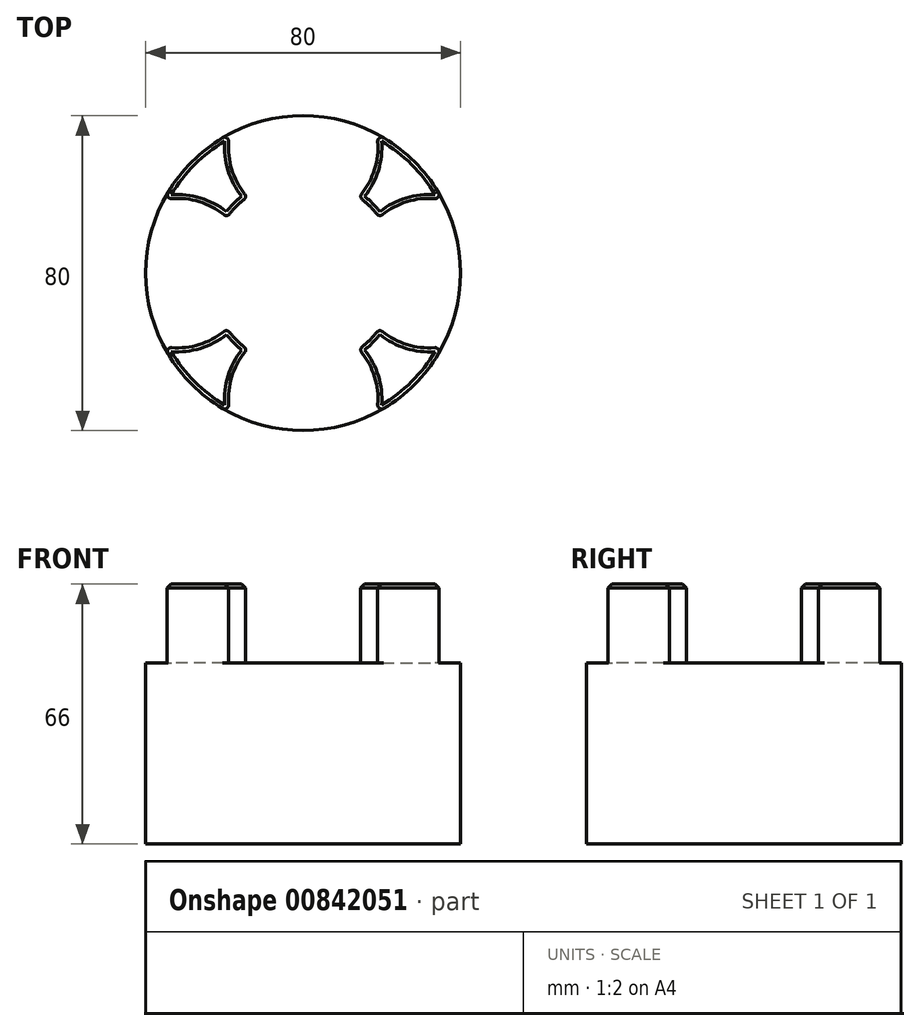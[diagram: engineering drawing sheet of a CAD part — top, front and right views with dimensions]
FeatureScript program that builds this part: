
annotation { "Feature Type Name" : "Feature", "Feature Type Description" : "" }
export const myFeature = defineFeature(function(context is Context, id is Id, definition is map)
    precondition{}
    {
        {
            var Q0;
            Q0=qCreatedBy(makeId("Top.planeOp"),FACE);
            var sketch = newSketch(context, id + "F0", { "sketchPlane" : qUnion([Q0])});
            skCircle(sketch, "E0", {"center": v(0, 0) * mm, "radius": 40 * mm});
            skSolve(sketch);
        }
        {
            var Q0;
            Q0=makeQuery(id+"F0.imprint","IMPRINT",FACE,{"disambiguationData":[TD([[makeQuery(id+"F0.imprint","IMPRINT",EDGE,{"derivedFrom":sQuery(id+"F0.wireOp",EDGE,"E0")}),1.0]])]});
            extrude(context, id + "F1", {"entities" : qUnion([Q0]), "depth" : 66 * mm, "offsetDistance" : 25 * mm});
        }
        {
            var Q0;
            Q0=makeQuery(id+"F1.opExtrude","CAP_FACE",FACE,{"disambiguationData":[OSD([sQuery(id+"F0.wireOp",EDGE,"E0")])],"isStart":false});
            var sketch = newSketch(context, id + "F2", { "sketchPlane" : qUnion([Q0])});
            skCircle(sketch, "E1", {"center": v(0, 0) * mm, "radius": 24 * mm});
            skSolve(sketch);
        }
        {
            var Q0;
            Q0=makeQuery(id+"F2.imprint","IMPRINT",FACE,{"disambiguationData":[TD([[makeQuery(id+"F2.imprint","IMPRINT",EDGE,{"derivedFrom":sQuery(id+"F2.wireOp",EDGE,"E1")}),1.0]])]});
            extrude(context, id + "F3", {"entities" : qUnion([Q0]), "operationType" : NewBodyOperationType.REMOVE, "oppositeDirection" : true, "depth" : 20 * mm, "offsetDistance" : 25 * mm});
        }
        {
            var Q0;
            Q0=makeQuery(id+"F1.opExtrude","CAP_FACE",FACE,{"disambiguationData":[OSD([sQuery(id+"F0.wireOp",EDGE,"E0")])],"isStart":false});
            var sketch = newSketch(context, id + "F4", { "sketchPlane" : qUnion([Q0])});
            skCircle(sketch, "E2", {"center": v(32, 0) * mm, "radius": 19 * mm});
            skCircle(sketch, "E3.1.0", {"center": v(0, 32) * mm, "radius": 19 * mm});
            skCircle(sketch, "E3.2.0", {"center": v(-32, 0) * mm, "radius": 19 * mm});
            skCircle(sketch, "E3.3.0", {"center": v(0, -32) * mm, "radius": 19 * mm});
            skPoint(sketch, "E3.center", {"position": v(0, 0) * mm});
            skSolve(sketch);
        }
        {
            var Q0;
            Q0 = qSketchRegion(id + "F4", true);
            extrude(context, id + "F5", {"entities" : qUnion([Q0]), "operationType" : NewBodyOperationType.REMOVE, "oppositeDirection" : true, "depth" : 20 * mm, "offsetDistance" : 25 * mm});
        }
        {
            var Q0;
            Q0=makeQuery(id+"F5.boolean.opBoolean","INTERSECT",EDGE,{"disambiguationData":[OD(1.0)],"derivedFrom":[makeQuery(id+"F1.opExtrude","SWEPT_FACE",FACE,{"disambiguationData":[OSD([sQuery(id+"F0.wireOp",EDGE,"E0")])]}),makeQuery(id+"F5.opExtrude","SWEPT_FACE",FACE,{"disambiguationData":[OSD([sQuery(id+"F4.wireOp",EDGE,"E3.1.0")])]})]});
            var Q1;
            Q1=makeQuery(id+"F5.boolean.opBoolean","INTERSECT",EDGE,{"disambiguationData":[OD(1.0)],"derivedFrom":[makeQuery(id+"F1.opExtrude","SWEPT_FACE",FACE,{"disambiguationData":[OSD([sQuery(id+"F0.wireOp",EDGE,"E0")])]}),makeQuery(id+"F5.opExtrude","SWEPT_FACE",FACE,{"disambiguationData":[OSD([sQuery(id+"F4.wireOp",EDGE,"E2")])]})]});
            var Q2;
            Q2=makeQuery(id+"F5.boolean.opBoolean","INTERSECT",EDGE,{"disambiguationData":[OD(1.0)],"derivedFrom":[makeQuery(id+"F3.boolean.opBoolean","COPY",FACE,{"derivedFrom":makeQuery(id+"F3.opExtrude","SWEPT_FACE",FACE,{"disambiguationData":[OSD([sQuery(id+"F2.wireOp",EDGE,"E1")])]})}),makeQuery(id+"F5.opExtrude","SWEPT_FACE",FACE,{"disambiguationData":[OSD([sQuery(id+"F4.wireOp",EDGE,"E2")])]})]});
            var Q3;
            Q3=makeQuery(id+"F5.boolean.opBoolean","INTERSECT",EDGE,{"disambiguationData":[OD(1.0)],"derivedFrom":[makeQuery(id+"F3.boolean.opBoolean","COPY",FACE,{"derivedFrom":makeQuery(id+"F3.opExtrude","SWEPT_FACE",FACE,{"disambiguationData":[OSD([sQuery(id+"F2.wireOp",EDGE,"E1")])]})}),makeQuery(id+"F5.opExtrude","SWEPT_FACE",FACE,{"disambiguationData":[OSD([sQuery(id+"F4.wireOp",EDGE,"E3.1.0")])]})]});
            var Q4;
            Q4=makeQuery(id+"F5.boolean.opBoolean","INTERSECT",EDGE,{"disambiguationData":[OD(0.0)],"derivedFrom":[makeQuery(id+"F3.boolean.opBoolean","COPY",FACE,{"derivedFrom":makeQuery(id+"F3.opExtrude","SWEPT_FACE",FACE,{"disambiguationData":[OSD([sQuery(id+"F2.wireOp",EDGE,"E1")])]})}),makeQuery(id+"F5.opExtrude","SWEPT_FACE",FACE,{"disambiguationData":[OSD([sQuery(id+"F4.wireOp",EDGE,"E2")])]})]});
            var Q5;
            Q5=makeQuery(id+"F5.boolean.opBoolean","INTERSECT",EDGE,{"disambiguationData":[OD(0.0)],"derivedFrom":[makeQuery(id+"F1.opExtrude","SWEPT_FACE",FACE,{"disambiguationData":[OSD([sQuery(id+"F0.wireOp",EDGE,"E0")])]}),makeQuery(id+"F5.opExtrude","SWEPT_FACE",FACE,{"disambiguationData":[OSD([sQuery(id+"F4.wireOp",EDGE,"E2")])]})]});
            var Q6;
            Q6=makeQuery(id+"F5.boolean.opBoolean","INTERSECT",EDGE,{"disambiguationData":[OD(1.0)],"derivedFrom":[makeQuery(id+"F1.opExtrude","SWEPT_FACE",FACE,{"disambiguationData":[OSD([sQuery(id+"F0.wireOp",EDGE,"E0")])]}),makeQuery(id+"F5.opExtrude","SWEPT_FACE",FACE,{"disambiguationData":[OSD([sQuery(id+"F4.wireOp",EDGE,"E3.3.0")])]})]});
            var Q7;
            Q7=makeQuery(id+"F5.boolean.opBoolean","INTERSECT",EDGE,{"disambiguationData":[OD(1.0)],"derivedFrom":[makeQuery(id+"F3.boolean.opBoolean","COPY",FACE,{"derivedFrom":makeQuery(id+"F3.opExtrude","SWEPT_FACE",FACE,{"disambiguationData":[OSD([sQuery(id+"F2.wireOp",EDGE,"E1")])]})}),makeQuery(id+"F5.opExtrude","SWEPT_FACE",FACE,{"disambiguationData":[OSD([sQuery(id+"F4.wireOp",EDGE,"E3.3.0")])]})]});
            var Q8;
            Q8=makeQuery(id+"F5.boolean.opBoolean","INTERSECT",EDGE,{"disambiguationData":[OD(0.0)],"derivedFrom":[makeQuery(id+"F1.opExtrude","SWEPT_FACE",FACE,{"disambiguationData":[OSD([sQuery(id+"F0.wireOp",EDGE,"E0")])]}),makeQuery(id+"F5.opExtrude","SWEPT_FACE",FACE,{"disambiguationData":[OSD([sQuery(id+"F4.wireOp",EDGE,"E3.3.0")])]})]});
            var Q9;
            Q9=makeQuery(id+"F5.boolean.opBoolean","INTERSECT",EDGE,{"disambiguationData":[OD(0.0)],"derivedFrom":[makeQuery(id+"F3.boolean.opBoolean","COPY",FACE,{"derivedFrom":makeQuery(id+"F3.opExtrude","SWEPT_FACE",FACE,{"disambiguationData":[OSD([sQuery(id+"F2.wireOp",EDGE,"E1")])]})}),makeQuery(id+"F5.opExtrude","SWEPT_FACE",FACE,{"disambiguationData":[OSD([sQuery(id+"F4.wireOp",EDGE,"E3.3.0")])]})]});
            var Q10;
            Q10=makeQuery(id+"F5.boolean.opBoolean","INTERSECT",EDGE,{"disambiguationData":[OD(1.0)],"derivedFrom":[makeQuery(id+"F1.opExtrude","SWEPT_FACE",FACE,{"disambiguationData":[OSD([sQuery(id+"F0.wireOp",EDGE,"E0")])]}),makeQuery(id+"F5.opExtrude","SWEPT_FACE",FACE,{"disambiguationData":[OSD([sQuery(id+"F4.wireOp",EDGE,"E3.2.0")])]})]});
            var Q11;
            Q11=makeQuery(id+"F5.boolean.opBoolean","INTERSECT",EDGE,{"disambiguationData":[OD(0.0)],"derivedFrom":[makeQuery(id+"F3.boolean.opBoolean","COPY",FACE,{"derivedFrom":makeQuery(id+"F3.opExtrude","SWEPT_FACE",FACE,{"disambiguationData":[OSD([sQuery(id+"F2.wireOp",EDGE,"E1")])]})}),makeQuery(id+"F5.opExtrude","SWEPT_FACE",FACE,{"disambiguationData":[OSD([sQuery(id+"F4.wireOp",EDGE,"E3.1.0")])]})]});
            var Q12;
            Q12=makeQuery(id+"F5.boolean.opBoolean","INTERSECT",EDGE,{"disambiguationData":[OD(1.0)],"derivedFrom":[makeQuery(id+"F3.boolean.opBoolean","COPY",FACE,{"derivedFrom":makeQuery(id+"F3.opExtrude","SWEPT_FACE",FACE,{"disambiguationData":[OSD([sQuery(id+"F2.wireOp",EDGE,"E1")])]})}),makeQuery(id+"F5.opExtrude","SWEPT_FACE",FACE,{"disambiguationData":[OSD([sQuery(id+"F4.wireOp",EDGE,"E3.2.0")])]})]});
            var Q13;
            Q13=makeQuery(id+"F5.boolean.opBoolean","INTERSECT",EDGE,{"disambiguationData":[OD(0.0)],"derivedFrom":[makeQuery(id+"F3.boolean.opBoolean","COPY",FACE,{"derivedFrom":makeQuery(id+"F3.opExtrude","SWEPT_FACE",FACE,{"disambiguationData":[OSD([sQuery(id+"F2.wireOp",EDGE,"E1")])]})}),makeQuery(id+"F5.opExtrude","SWEPT_FACE",FACE,{"disambiguationData":[OSD([sQuery(id+"F4.wireOp",EDGE,"E3.2.0")])]})]});
            var Q14;
            Q14=makeQuery(id+"F5.boolean.opBoolean","INTERSECT",EDGE,{"disambiguationData":[OD(0.0)],"derivedFrom":[makeQuery(id+"F1.opExtrude","SWEPT_FACE",FACE,{"disambiguationData":[OSD([sQuery(id+"F0.wireOp",EDGE,"E0")])]}),makeQuery(id+"F5.opExtrude","SWEPT_FACE",FACE,{"disambiguationData":[OSD([sQuery(id+"F4.wireOp",EDGE,"E3.2.0")])]})]});
            var Q15;
            Q15=makeQuery(id+"F5.boolean.opBoolean","INTERSECT",EDGE,{"disambiguationData":[OD(0.0)],"derivedFrom":[makeQuery(id+"F1.opExtrude","SWEPT_FACE",FACE,{"disambiguationData":[OSD([sQuery(id+"F0.wireOp",EDGE,"E0")])]}),makeQuery(id+"F5.opExtrude","SWEPT_FACE",FACE,{"disambiguationData":[OSD([sQuery(id+"F4.wireOp",EDGE,"E3.1.0")])]})]});
            fillet(context, id + "F6", {"entities" : qUnion([Q0, Q1, Q2, Q3, Q4, Q5, Q6, Q7, Q8, Q9, Q10, Q11, Q12, Q13, Q14, Q15]), "radius" : 1 * mm, "tangentPropagation" : true, "allowEdgeOverflow" : false});
        }
        {
            var Q0;
            {var subQ0=sQuery(id+"F0.wireOp",EDGE,"E0");Q0=makeQuery(id+"F5.boolean.opBoolean","SPLIT",FACE,{"disambiguationData":[TD([makeQuery(id+"F1.opExtrude","SWEPT_FACE",FACE,{"disambiguationData":[OSD([subQ0])]}),makeQuery(id+"F3.boolean.opBoolean","COPY",FACE,{"derivedFrom":makeQuery(id+"F3.opExtrude","SWEPT_FACE",FACE,{"disambiguationData":[OSD([sQuery(id+"F2.wireOp",EDGE,"E1")])]})}),makeQuery(id+"F5.opExtrude","SWEPT_FACE",FACE,{"disambiguationData":[OSD([sQuery(id+"F4.wireOp",EDGE,"E2")])]}),makeQuery(id+"F5.opExtrude","SWEPT_FACE",FACE,{"disambiguationData":[OSD([sQuery(id+"F4.wireOp",EDGE,"E3.1.0")])]})])],"derivedFrom":makeQuery(id+"F1.opExtrude","CAP_FACE",FACE,{"disambiguationData":[OSD([subQ0])],"isStart":false})});}
            var Q1;
            {var subQ0=sQuery(id+"F0.wireOp",EDGE,"E0");Q1=makeQuery(id+"F5.boolean.opBoolean","SPLIT",FACE,{"disambiguationData":[TD([makeQuery(id+"F1.opExtrude","SWEPT_FACE",FACE,{"disambiguationData":[OSD([subQ0])]}),makeQuery(id+"F3.boolean.opBoolean","COPY",FACE,{"derivedFrom":makeQuery(id+"F3.opExtrude","SWEPT_FACE",FACE,{"disambiguationData":[OSD([sQuery(id+"F2.wireOp",EDGE,"E1")])]})}),makeQuery(id+"F5.opExtrude","SWEPT_FACE",FACE,{"disambiguationData":[OSD([sQuery(id+"F4.wireOp",EDGE,"E2")])]}),makeQuery(id+"F5.opExtrude","SWEPT_FACE",FACE,{"disambiguationData":[OSD([sQuery(id+"F4.wireOp",EDGE,"E3.3.0")])]})])],"derivedFrom":makeQuery(id+"F1.opExtrude","CAP_FACE",FACE,{"disambiguationData":[OSD([subQ0])],"isStart":false})});}
            var Q2;
            {var subQ0=sQuery(id+"F0.wireOp",EDGE,"E0");Q2=makeQuery(id+"F5.boolean.opBoolean","SPLIT",FACE,{"disambiguationData":[TD([makeQuery(id+"F1.opExtrude","SWEPT_FACE",FACE,{"disambiguationData":[OSD([subQ0])]}),makeQuery(id+"F3.boolean.opBoolean","COPY",FACE,{"derivedFrom":makeQuery(id+"F3.opExtrude","SWEPT_FACE",FACE,{"disambiguationData":[OSD([sQuery(id+"F2.wireOp",EDGE,"E1")])]})}),makeQuery(id+"F5.opExtrude","SWEPT_FACE",FACE,{"disambiguationData":[OSD([sQuery(id+"F4.wireOp",EDGE,"E3.1.0")])]}),makeQuery(id+"F5.opExtrude","SWEPT_FACE",FACE,{"disambiguationData":[OSD([sQuery(id+"F4.wireOp",EDGE,"E3.2.0")])]})])],"derivedFrom":makeQuery(id+"F1.opExtrude","CAP_FACE",FACE,{"disambiguationData":[OSD([subQ0])],"isStart":false})});}
            var Q3;
            {var subQ0=sQuery(id+"F0.wireOp",EDGE,"E0");Q3=makeQuery(id+"F5.boolean.opBoolean","SPLIT",FACE,{"disambiguationData":[TD([makeQuery(id+"F1.opExtrude","SWEPT_FACE",FACE,{"disambiguationData":[OSD([subQ0])]}),makeQuery(id+"F3.boolean.opBoolean","COPY",FACE,{"derivedFrom":makeQuery(id+"F3.opExtrude","SWEPT_FACE",FACE,{"disambiguationData":[OSD([sQuery(id+"F2.wireOp",EDGE,"E1")])]})}),makeQuery(id+"F5.opExtrude","SWEPT_FACE",FACE,{"disambiguationData":[OSD([sQuery(id+"F4.wireOp",EDGE,"E3.2.0")])]}),makeQuery(id+"F5.opExtrude","SWEPT_FACE",FACE,{"disambiguationData":[OSD([sQuery(id+"F4.wireOp",EDGE,"E3.3.0")])]})])],"derivedFrom":makeQuery(id+"F1.opExtrude","CAP_FACE",FACE,{"disambiguationData":[OSD([subQ0])],"isStart":false})});}
            chamfer(context, id + "F7", {"entities" : qUnion([Q0, Q1, Q2, Q3]), "width" : 1 * mm, "tangentPropagation" : true});
        }
    });
